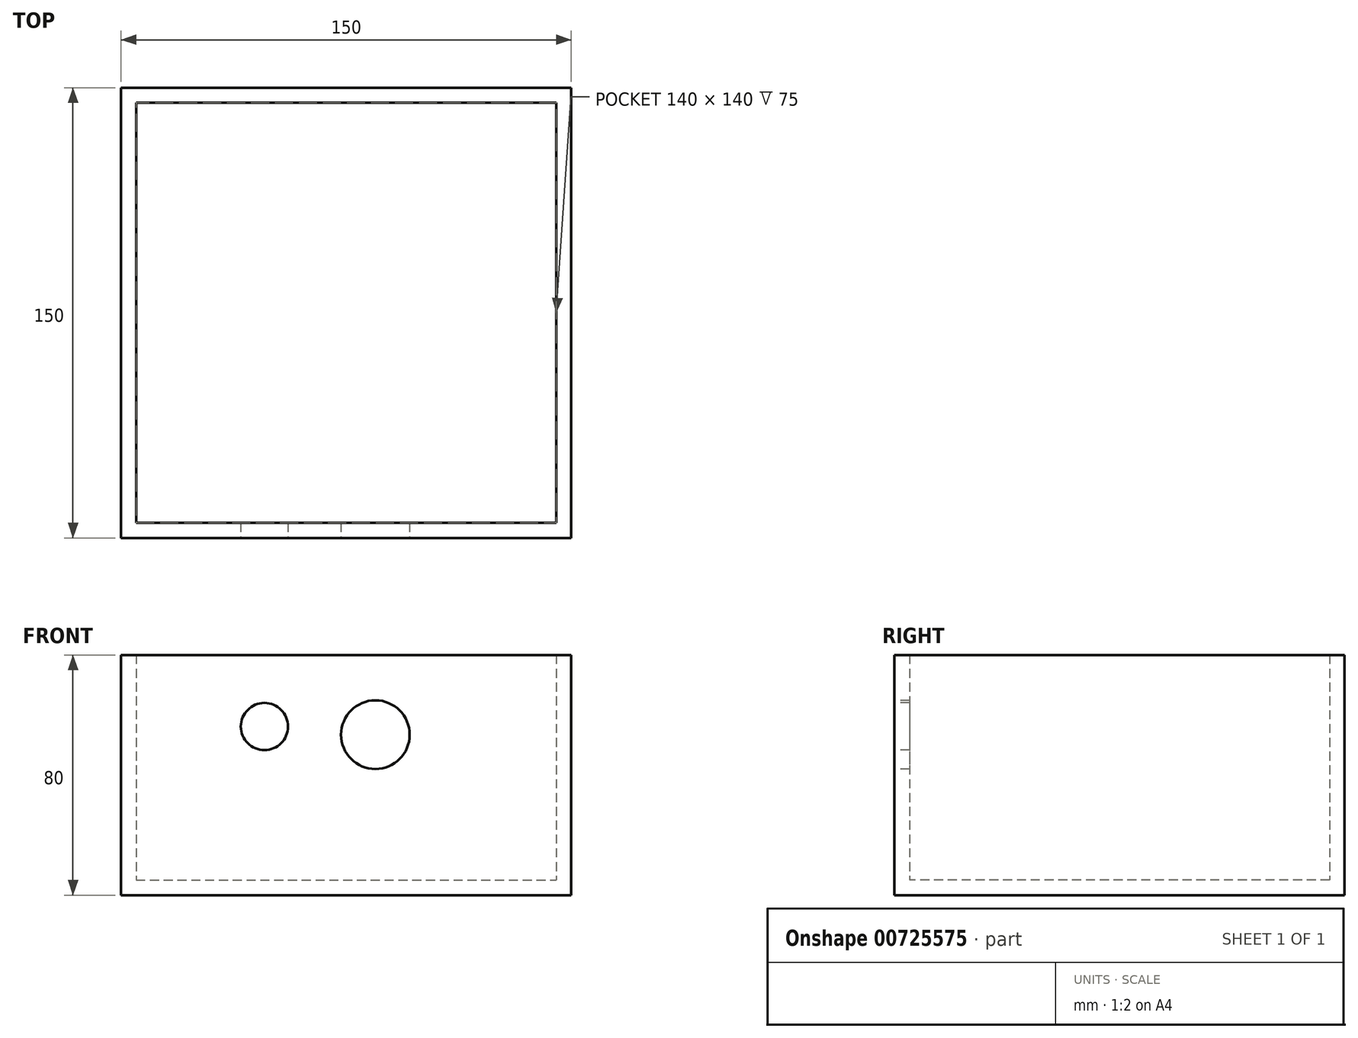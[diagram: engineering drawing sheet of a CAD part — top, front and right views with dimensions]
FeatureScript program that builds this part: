
annotation { "Feature Type Name" : "Feature", "Feature Type Description" : "" }
export const myFeature = defineFeature(function(context is Context, id is Id, definition is map)
    precondition{}
    {
        {
            var Q0;
            Q0=qCreatedBy(makeId("Top.planeOp"),FACE);
            var sketch = newSketch(context, id + "F0", { "sketchPlane" : qUnion([Q0])});
            skLineSegment(sketch, "E0.bottom", {"start": v(-75, 75) * mm, "end": v(75, 75) * mm});
            skLineSegment(sketch, "E0.top", {"start": v(-75, -75) * mm, "end": v(75, -75) * mm});
            skLineSegment(sketch, "E0.left", {"start": v(-75, 75) * mm, "end": v(-75, -75) * mm});
            skLineSegment(sketch, "E0.right", {"start": v(75, 75) * mm, "end": v(75, -75) * mm});
            skLineSegment(sketch, "E1", {"start": v(0, 75) * mm, "end": v(0, 0) * mm, "construction": true});
            skLineSegment(sketch, "E2", {"start": v(0, 0) * mm, "end": v(75, 0) * mm, "construction": true});
            skSolve(sketch);
        }
        {
            var Q0;
            Q0 = qSketchRegion(id + "F0", true);
            extrude(context, id + "F1", {"entities" : qUnion([Q0]), "depth" : 80 * mm, "offsetDistance" : 25.4 * mm});
        }
        {
            var Q0;
            Q0=makeQuery(id+"F1.opExtrude","CAP_FACE",FACE,{"disambiguationData":[OSD([sQuery(id+"F0.wireOp",EDGE,"E0.bottom"),sQuery(id+"F0.wireOp",EDGE,"E0.top"),sQuery(id+"F0.wireOp",EDGE,"E0.left"),sQuery(id+"F0.wireOp",EDGE,"E0.right")])],"isStart":false});
            shell(context, id + "F2", {"entities" : qUnion([Q0]), "thickness" : 5 * mm});
        }
        {
            var Q0;
            Q0=makeQuery(id+"F1.opExtrude","SWEPT_FACE",FACE,{"disambiguationData":[OSD([sQuery(id+"F0.wireOp",EDGE,"E0.top")])]});
            var sketch = newSketch(context, id + "F3", { "sketchPlane" : qUnion([Q0])});
            skCircle(sketch, "E3", {"center": v(-27.25, 56.16) * mm, "radius": 7.86 * mm});
            skCircle(sketch, "E4", {"center": v(9.72, 53.46) * mm, "radius": 11.43 * mm});
            skSolve(sketch);
        }
        {
            var Q0;
            Q0 = qSketchRegion(id + "F3", true);
            extrude(context, id + "F4", {"entities" : qUnion([Q0]), "operationType" : NewBodyOperationType.REMOVE, "oppositeDirection" : true, "depth" : 25 * mm, "offsetDistance" : 25 * mm});
        }
    });
